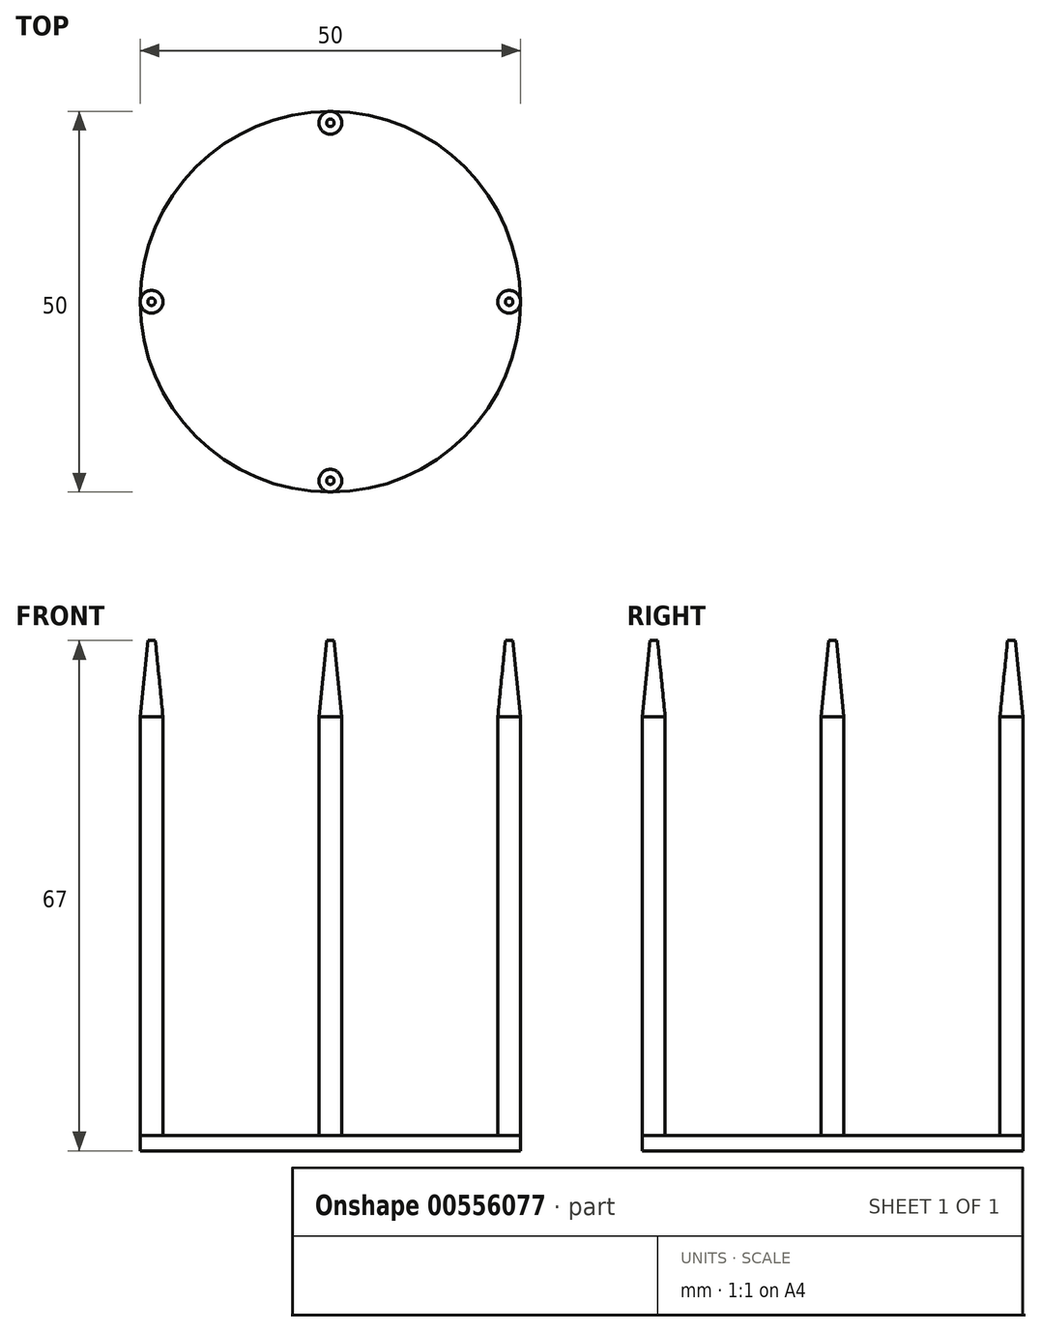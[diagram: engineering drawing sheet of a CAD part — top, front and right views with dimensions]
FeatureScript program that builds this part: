
annotation { "Feature Type Name" : "Feature", "Feature Type Description" : "" }
export const myFeature = defineFeature(function(context is Context, id is Id, definition is map)
    precondition{}
    {
        {
            var Q0;
            Q0=qCreatedBy(makeId("Top.planeOp"),FACE);
            var sketch = newSketch(context, id + "F0", { "sketchPlane" : qUnion([Q0])});
            skCircle(sketch, "E0", {"center": v(0, 0) * mm, "radius": 25 * mm});
            skSolve(sketch);
        }
        {
            var Q0;
            Q0=makeQuery(id+"F0.imprint","IMPRINT",FACE,{"disambiguationData":[TD([[makeQuery(id+"F0.imprint","IMPRINT",EDGE,{"derivedFrom":sQuery(id+"F0.wireOp",EDGE,"E0")}),1.0]])]});
            extrude(context, id + "F1", {"entities" : qUnion([Q0]), "depth" : 2 * mm, "offsetDistance" : 25 * mm});
        }
        {
            var Q0;
            Q0=makeQuery(id+"F1.opExtrude","CAP_FACE",FACE,{"disambiguationData":[OSD([sQuery(id+"F0.wireOp",EDGE,"E0")])],"isStart":false});
            var sketch = newSketch(context, id + "F2", { "sketchPlane" : qUnion([Q0])});
            skLineSegment(sketch, "E1", {"start": v(-25, 0) * mm, "end": v(-23.5, 0) * mm, "construction": true});
            skCircle(sketch, "E2", {"center": v(-23.5, 0) * mm, "radius": 1.5 * mm});
            skSolve(sketch);
        }
        {
            var Q0;
            Q0=makeQuery(id+"F2.imprint","IMPRINT",FACE,{"disambiguationData":[TD([[makeQuery(id+"F2.imprint","IMPRINT",EDGE,{"derivedFrom":sQuery(id+"F2.wireOp",EDGE,"E2")}),1.0]])]});
            extrude(context, id + "F3", {"entities" : qUnion([Q0]), "operationType" : NewBodyOperationType.ADD, "depth" : 65 * mm, "offsetDistance" : 25 * mm});
        }
        {
            var Q0;
            Q0=makeQuery(id+"F3.opExtrude","CAP_EDGE",EDGE,{"disambiguationData":[OSD([sQuery(id+"F2.wireOp",EDGE,"E2")])],"isStart":false});
            chamfer(context, id + "F4", {"entities" : qUnion([Q0]), "chamferType" : ChamferType.TWO_OFFSETS, "width1" : 1 * mm, "oppositeDirection" : false, "width2" : 10 * mm, "tangentPropagation" : true});
        }
        {
            var Q0;
            Q0=makeQuery(id+"F1.opExtrude","SWEPT_BODY",BODY,{"disambiguationData":[OSD([sQuery(id+"F0.wireOp",EDGE,"E0")])]});
            var Q1;
            Q1=makeQuery(id+"F1.opExtrude","CAP_EDGE",EDGE,{"disambiguationData":[OSD([sQuery(id+"F0.wireOp",EDGE,"E0")])],"isStart":false});
            circularPattern(context, id + "F5", {"entities" : qUnion([Q0]), "axis" : qUnion([Q1]), "angle" : 360 * degree, "instanceCount" : 4, "equalSpace" : true});
        }
    });
